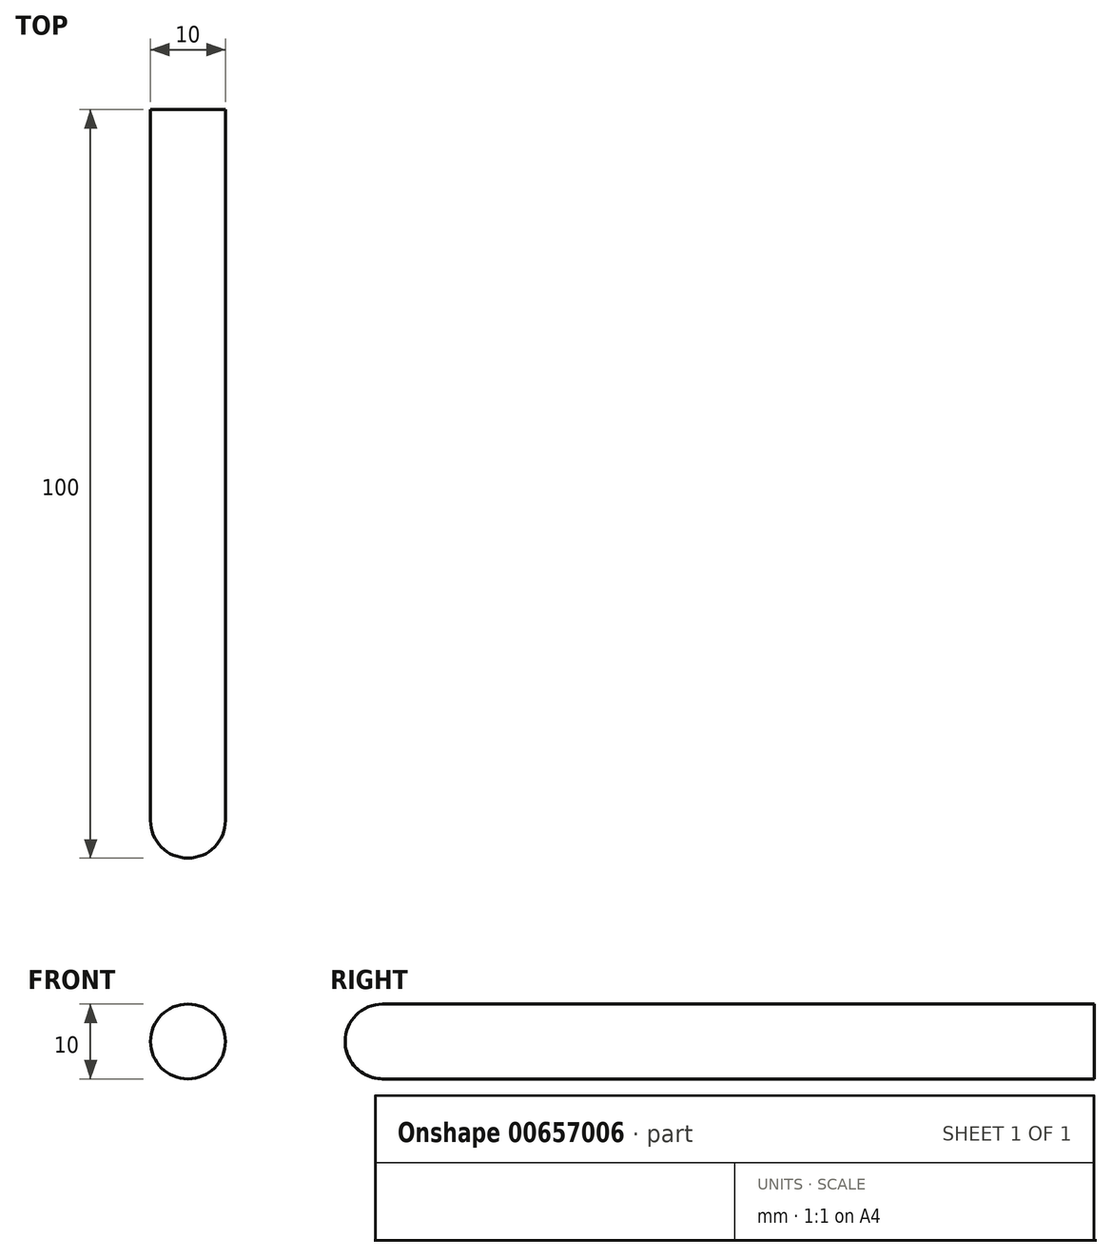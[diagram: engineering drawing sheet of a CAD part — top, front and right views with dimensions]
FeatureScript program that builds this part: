
annotation { "Feature Type Name" : "Feature", "Feature Type Description" : "" }
export const myFeature = defineFeature(function(context is Context, id is Id, definition is map)
    precondition{}
    {
        {
            var Q0;
            Q0=qCreatedBy(makeId("Front.planeOp"),FACE);
            var sketch = newSketch(context, id + "F0", { "sketchPlane" : qUnion([Q0])});
            skLineSegment(sketch, "E0.bottom", {"start": v(-110.6, 37.96) * mm, "end": v(-100.6, 37.96) * mm});
            skLineSegment(sketch, "E0.top", {"start": v(-110.6, 27.96) * mm, "end": v(-100.6, 27.96) * mm});
            skLineSegment(sketch, "E0.left", {"start": v(-110.6, 37.96) * mm, "end": v(-110.6, 27.96) * mm});
            skLineSegment(sketch, "E0.right", {"start": v(-100.6, 37.96) * mm, "end": v(-100.6, 27.96) * mm});
            skSolve(sketch);
        }
        {
            var Q0;
            Q0=makeQuery(id+"F0.imprint","IMPRINT",FACE,{"disambiguationData":[TD([[makeQuery(id+"F0.imprint","IMPRINT",EDGE,{"derivedFrom":sQuery(id+"F0.wireOp",EDGE,"E0.bottom")}),-1.0]])]});
            extrude(context, id + "F1", {"entities" : qUnion([Q0]), "depth" : 100 * mm, "offsetDistance" : 25.4 * mm});
        }
        {
            var Q0;
            Q0=makeQuery(id+"F1.opExtrude","SWEPT_EDGE",EDGE,{"disambiguationData":[OSD([sQuery(id+"F0.wireOp",EDGE,"E0.bottom"),sQuery(id+"F0.wireOp",EDGE,"E0.left")])]});
            var Q1;
            Q1=makeQuery(id+"F1.opExtrude","SWEPT_EDGE",EDGE,{"disambiguationData":[OSD([sQuery(id+"F0.wireOp",EDGE,"E0.bottom"),sQuery(id+"F0.wireOp",EDGE,"E0.right")])]});
            var Q2;
            Q2=makeQuery(id+"F1.opExtrude","SWEPT_EDGE",EDGE,{"disambiguationData":[OSD([sQuery(id+"F0.wireOp",EDGE,"E0.top"),sQuery(id+"F0.wireOp",EDGE,"E0.right")])]});
            var Q3;
            Q3=makeQuery(id+"F1.opExtrude","SWEPT_EDGE",EDGE,{"disambiguationData":[OSD([sQuery(id+"F0.wireOp",EDGE,"E0.top"),sQuery(id+"F0.wireOp",EDGE,"E0.left")])]});
            fillet(context, id + "F2", {"entities" : qUnion([Q0, Q1, Q2, Q3]), "radius" : 5 * mm, "tangentPropagation" : true, "allowEdgeOverflow" : false});
        }
        {
            var Q0;
            {var subQ0=sQuery(id+"F0.wireOp",EDGE,"E0.left");var subQ1=sQuery(id+"F0.wireOp",EDGE,"E0.bottom");Q0=makeQuery(id+"F2.opFillet","BLEND_EDGE",EDGE,{"blendedFrom":[makeQuery(id+"F1.opExtrude","SWEPT_EDGE",EDGE,{"disambiguationData":[OSD([subQ1,subQ0])]}),makeQuery(id+"F1.opExtrude","CAP_FACE",FACE,{"disambiguationData":[OSD([subQ1,sQuery(id+"F0.wireOp",EDGE,"E0.top"),subQ0,sQuery(id+"F0.wireOp",EDGE,"E0.right")])],"isStart":false})],"blendedInto":[makeQuery(id+"F1.opExtrude","CAP_FACE",FACE,{"disambiguationData":[OSD([subQ1,sQuery(id+"F0.wireOp",EDGE,"E0.top"),subQ0,sQuery(id+"F0.wireOp",EDGE,"E0.right")])],"isStart":false})]});}
            fillet(context, id + "F3", {"entities" : qUnion([Q0]), "radius" : 5 * mm, "tangentPropagation" : true, "allowEdgeOverflow" : false});
        }
    });
